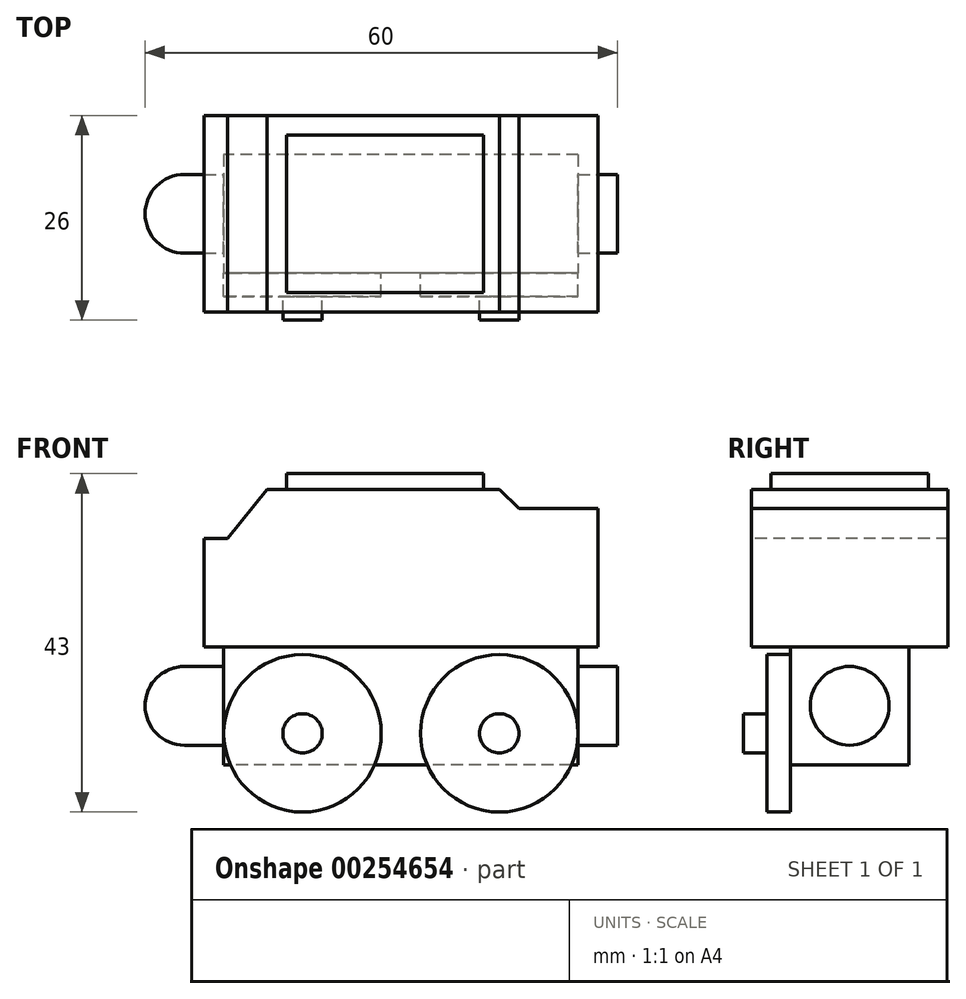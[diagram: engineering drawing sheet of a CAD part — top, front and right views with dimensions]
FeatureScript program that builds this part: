
annotation { "Feature Type Name" : "Feature", "Feature Type Description" : "" }
export const myFeature = defineFeature(function(context is Context, id is Id, definition is map)
    precondition{}
    {
        {
            var Q0;
            Q0=qCreatedBy(makeId("Top.planeOp"),FACE);
            var sketch = newSketch(context, id + "F0", { "sketchPlane" : qUnion([Q0])});
            skLineSegment(sketch, "E0.bottom", {"start": v(22.5, 7.5) * mm, "end": v(-22.5, 7.5) * mm});
            skLineSegment(sketch, "E0.top", {"start": v(22.5, -7.5) * mm, "end": v(-22.5, -7.5) * mm});
            skLineSegment(sketch, "E0.left", {"start": v(22.5, 7.5) * mm, "end": v(22.5, -7.5) * mm});
            skLineSegment(sketch, "E0.right", {"start": v(-22.5, 7.5) * mm, "end": v(-22.5, -7.5) * mm});
            skPoint(sketch, "E0.middle", {"position": v(0, 0) * mm});
            skSolve(sketch);
        }
        {
            var Q0;
            Q0 = qSketchRegion(id + "F0", true);
            extrude(context, id + "F1", {"entities" : qUnion([Q0]), "endBound" : BoundingType.SYMMETRIC, "depth" : 15 * mm});
        }
        {
            var Q0;
            Q0=makeQuery(id+"F1.opExtrude","CAP_FACE",FACE,{"disambiguationData":[OSD([sQuery(id+"F0.wireOp",EDGE,"E0.bottom"),sQuery(id+"F0.wireOp",EDGE,"E0.top"),sQuery(id+"F0.wireOp",EDGE,"E0.left"),sQuery(id+"F0.wireOp",EDGE,"E0.right")])],"isStart":false});
            var sketch = newSketch(context, id + "F2", { "sketchPlane" : qUnion([Q0])});
            skLineSegment(sketch, "E1.bottom", {"start": v(25, 12.5) * mm, "end": v(-25, 12.5) * mm});
            skLineSegment(sketch, "E1.top", {"start": v(25, -12.5) * mm, "end": v(-25, -12.5) * mm});
            skLineSegment(sketch, "E1.left", {"start": v(25, 12.5) * mm, "end": v(25, -12.5) * mm});
            skLineSegment(sketch, "E1.right", {"start": v(-25, 12.5) * mm, "end": v(-25, -12.5) * mm});
            skPoint(sketch, "E1.middle", {"position": v(0, 0) * mm});
            skSolve(sketch);
        }
        {
            var Q0;
            Q0 = qSketchRegion(id + "F2", true);
            extrude(context, id + "F3", {"entities" : qUnion([Q0]), "operationType" : NewBodyOperationType.ADD, "depth" : 20 * mm});
        }
        {
            var Q0;
            Q0=makeQuery(id+"F3.opExtrude","SWEPT_FACE",FACE,{"disambiguationData":[OSD([sQuery(id+"F2.wireOp",EDGE,"E1.top")])]});
            var sketch = newSketch(context, id + "F4", { "sketchPlane" : qUnion([Q0])});
            skLineSegment(sketch, "E2", {"start": v(12.5, 27.5) * mm, "end": v(15, 25.05) * mm});
            skLineSegment(sketch, "E3", {"start": v(15, 25.05) * mm, "end": v(25, 25.05) * mm});
            skLineSegment(sketch, "E4", {"start": v(25, 25.05) * mm, "end": v(25, 27.5) * mm});
            skLineSegment(sketch, "E5", {"start": v(25, 27.5) * mm, "end": v(12.5, 27.5) * mm});
            skSolve(sketch);
        }
        {
            var Q0;
            Q0 = qSketchRegion(id + "F4", true);
            var Q1;
            Q1=makeQuery(id+"F3.opExtrude","SWEPT_FACE",FACE,{"disambiguationData":[OSD([sQuery(id+"F2.wireOp",EDGE,"E1.bottom")])]});
            extrude(context, id + "F5", {"entities" : qUnion([Q0]), "operationType" : NewBodyOperationType.REMOVE, "endBound" : BoundingType.UP_TO_SURFACE, "oppositeDirection" : true, "endBoundEntityFace" : qUnion([Q1]), "depth" : 25 * mm});
        }
        {
            var Q0;
            Q0=makeQuery(id+"F3.opExtrude","SWEPT_FACE",FACE,{"disambiguationData":[OSD([sQuery(id+"F2.wireOp",EDGE,"E1.top")])]});
            var sketch = newSketch(context, id + "F6", { "sketchPlane" : qUnion([Q0])});
            skLineSegment(sketch, "E6", {"start": v(-25, 21.26) * mm, "end": v(-22, 21.26) * mm});
            skLineSegment(sketch, "E7", {"start": v(-22, 21.26) * mm, "end": v(-17, 27.5) * mm});
            skLineSegment(sketch, "E8", {"start": v(-17, 27.5) * mm, "end": v(-25, 27.5) * mm});
            skLineSegment(sketch, "E9", {"start": v(-25, 27.5) * mm, "end": v(-25, 21.26) * mm});
            skSolve(sketch);
        }
        {
            var Q0;
            Q0 = qSketchRegion(id + "F6", true);
            var Q1;
            Q1=makeQuery(id+"F3.opExtrude","SWEPT_FACE",FACE,{"disambiguationData":[OSD([sQuery(id+"F2.wireOp",EDGE,"E1.bottom")])]});
            extrude(context, id + "F7", {"entities" : qUnion([Q0]), "operationType" : NewBodyOperationType.REMOVE, "endBound" : BoundingType.UP_TO_SURFACE, "oppositeDirection" : true, "endBoundEntityFace" : qUnion([Q1]), "depth" : 25 * mm});
        }
        {
            var Q0;
            Q0=makeQuery(id+"F3.opExtrude","CAP_FACE",FACE,{"disambiguationData":[OSD([sQuery(id+"F2.wireOp",EDGE,"E1.bottom"),sQuery(id+"F2.wireOp",EDGE,"E1.top"),sQuery(id+"F2.wireOp",EDGE,"E1.left"),sQuery(id+"F2.wireOp",EDGE,"E1.right")])],"isStart":false});
            var sketch = newSketch(context, id + "F8", { "sketchPlane" : qUnion([Q0])});
            skLineSegment(sketch, "E10.bottom", {"start": v(-14.5, 10) * mm, "end": v(10.5, 10) * mm});
            skLineSegment(sketch, "E10.top", {"start": v(-14.5, -10) * mm, "end": v(10.5, -10) * mm});
            skLineSegment(sketch, "E10.left", {"start": v(-14.5, 10) * mm, "end": v(-14.5, -10) * mm});
            skLineSegment(sketch, "E10.right", {"start": v(10.5, 10) * mm, "end": v(10.5, -10) * mm});
            skSolve(sketch);
        }
        {
            var Q0;
            Q0 = qSketchRegion(id + "F8", true);
            extrude(context, id + "F9", {"entities" : qUnion([Q0]), "operationType" : NewBodyOperationType.ADD, "depth" : 2 * mm});
        }
        {
            var Q0;
            Q0=qCreatedBy(makeId("Front.planeOp"),FACE);
            var sketch = newSketch(context, id + "F10", { "sketchPlane" : qUnion([Q0])});
            skLineSegment(sketch, "E11", {"start": v(49.97, 0) * mm, "end": v(-66.93, 0) * mm, "construction": true});
            skSolve(sketch);
        }
        {
            var Q0;
            Q0=qCreatedBy(makeId("Front.planeOp"),FACE);
            var sketch = newSketch(context, id + "F11", { "sketchPlane" : qUnion([Q0])});
            skLineSegment(sketch, "E12.bottom", {"start": v(22.5, 0) * mm, "end": v(27.5, 0) * mm});
            skLineSegment(sketch, "E12.top", {"start": v(22.5, -5) * mm, "end": v(27.5, -5) * mm});
            skLineSegment(sketch, "E12.left", {"start": v(22.5, 0) * mm, "end": v(22.5, -5) * mm});
            skLineSegment(sketch, "E12.right", {"start": v(27.5, 0) * mm, "end": v(27.5, -5) * mm});
            skSolve(sketch);
        }
        {
            var Q0;
            Q0 = qSketchRegion(id + "F11", true);
            var Q1;
            Q1=sQuery(id+"F10.wireOp",EDGE,"E11");
            revolve(context, id + "F12", {"operationType" : NewBodyOperationType.ADD, "entities" : qUnion([Q0]), "axis" : qUnion([Q1]), "revolveType" : RevolveType.FULL});
        }
        {
            var Q0;
            Q0=qCreatedBy(makeId("Front.planeOp"),FACE);
            var sketch = newSketch(context, id + "F13", { "sketchPlane" : qUnion([Q0])});
            skLineSegment(sketch, "E13.bottom", {"start": v(-22.5, 0) * mm, "end": v(-27.5, 0) * mm});
            skLineSegment(sketch, "E13.top", {"start": v(-22.5, -5) * mm, "end": v(-27.5, -5) * mm});
            skLineSegment(sketch, "E13.left", {"start": v(-22.5, 0) * mm, "end": v(-22.5, -5) * mm});
            skLineSegment(sketch, "E13.right", {"start": v(-27.5, 0) * mm, "end": v(-27.5, -5) * mm});
            skSolve(sketch);
        }
        {
            var Q0;
            Q0 = qSketchRegion(id + "F13", true);
            var Q1;
            Q1=sQuery(id+"F10.wireOp",EDGE,"E11");
            revolve(context, id + "F14", {"operationType" : NewBodyOperationType.ADD, "entities" : qUnion([Q0]), "axis" : qUnion([Q1]), "revolveType" : RevolveType.FULL});
        }
        {
            var Q0;
            Q0=makeQuery(id+"F1.opExtrude","SWEPT_FACE",FACE,{"disambiguationData":[OSD([sQuery(id+"F0.wireOp",EDGE,"E0.top")])]});
            var sketch = newSketch(context, id + "F15", { "sketchPlane" : qUnion([Q0])});
            skCircle(sketch, "E14", {"center": v(-12.5, -3.5) * mm, "radius": 10 * mm});
            skSolve(sketch);
        }
        {
            var Q0;
            Q0 = qSketchRegion(id + "F15", true);
            extrude(context, id + "F16", {"entities" : qUnion([Q0]), "operationType" : NewBodyOperationType.ADD, "depth" : 3 * mm});
        }
        {
            var Q0;
            {var subQ0=sQuery(id+"F0.wireOp",EDGE,"E0.right");var subQ1=sQuery(id+"F0.wireOp",EDGE,"E0.left");var subQ2=sQuery(id+"F0.wireOp",EDGE,"E0.top");var subQ3=makeQuery(id+"F1.opExtrude","SWEPT_FACE",FACE,{"disambiguationData":[OSD([subQ2])]});var subQ4=sQuery(id+"F15.wireOp",EDGE,"E14");Q0=makeQuery(id+"F16.boolean.opBoolean","SPLIT",FACE,{"disambiguationData":[TD([makeQuery(id+"F1.opExtrude","CAP_FACE",FACE,{"disambiguationData":[OSD([sQuery(id+"F0.wireOp",EDGE,"E0.bottom"),subQ2,subQ1,subQ0])],"isStart":true}),subQ3,makeQuery(id+"F1.opExtrude","SWEPT_FACE",FACE,{"disambiguationData":[OSD([subQ1])]}),makeQuery(id+"F1.opExtrude","SWEPT_FACE",FACE,{"disambiguationData":[OSD([subQ0])]}),makeQuery(id+"F3.opExtrude","CAP_FACE",FACE,{"disambiguationData":[OSD([sQuery(id+"F2.wireOp",EDGE,"E1.bottom"),sQuery(id+"F2.wireOp",EDGE,"E1.top"),sQuery(id+"F2.wireOp",EDGE,"E1.left"),sQuery(id+"F2.wireOp",EDGE,"E1.right")])],"isStart":true}),makeQuery(id+"F16.opExtrude","SWEPT_FACE",FACE,{"disambiguationData":[OSD([subQ4])]}),makeQuery(id+"F16.opExtrude","CAP_FACE",FACE,{"disambiguationData":[OSD([subQ4])],"isStart":true})])],"derivedFrom":subQ3});}
            var sketch = newSketch(context, id + "F17", { "sketchPlane" : qUnion([Q0])});
            skCircle(sketch, "E15", {"center": v(12.5, -3.5) * mm, "radius": 10 * mm});
            skSolve(sketch);
        }
        {
            var Q0;
            Q0 = qSketchRegion(id + "F17", true);
            extrude(context, id + "F18", {"entities" : qUnion([Q0]), "operationType" : NewBodyOperationType.ADD, "depth" : 3 * mm});
        }
        {
            var Q0;
            Q0=makeQuery(id+"F16.opExtrude","CAP_FACE",FACE,{"disambiguationData":[OSD([sQuery(id+"F15.wireOp",EDGE,"E14")])],"isStart":false});
            var sketch = newSketch(context, id + "F19", { "sketchPlane" : qUnion([Q0])});
            skCircle(sketch, "E16", {"center": v(-12.5, -3.5) * mm, "radius": 2.5 * mm});
            skSolve(sketch);
        }
        {
            var Q0;
            Q0 = qSketchRegion(id + "F19", true);
            extrude(context, id + "F20", {"entities" : qUnion([Q0]), "operationType" : NewBodyOperationType.ADD, "depth" : 3 * mm});
        }
        {
            var Q0;
            Q0=makeQuery(id+"F18.opExtrude","CAP_FACE",FACE,{"disambiguationData":[OSD([sQuery(id+"F17.wireOp",EDGE,"E15")])],"isStart":false});
            var sketch = newSketch(context, id + "F21", { "sketchPlane" : qUnion([Q0])});
            skCircle(sketch, "E17", {"center": v(12.5, -3.5) * mm, "radius": 2.5 * mm});
            skSolve(sketch);
        }
        {
            var Q0;
            Q0 = qSketchRegion(id + "F21", true);
            extrude(context, id + "F22", {"entities" : qUnion([Q0]), "operationType" : NewBodyOperationType.ADD, "depth" : 3 * mm});
        }
        {
            var Q0;
            Q0=qCreatedBy(makeId("Front.planeOp"),FACE);
            var sketch = newSketch(context, id + "F23", { "sketchPlane" : qUnion([Q0])});
            skArc(sketch, "E18", {"start": v(-27.5, 5) * mm, "mid": v(-31.04, 3.54) * mm, "end": v(-32.5, 0) * mm});
            skLineSegment(sketch, "E19", {"start": v(-32.5, 0) * mm, "end": v(-27.5, 0) * mm});
            skLineSegment(sketch, "E20", {"start": v(-27.5, 0) * mm, "end": v(-27.5, 5) * mm});
            skSolve(sketch);
        }
        {
            var Q0;
            Q0 = qSketchRegion(id + "F23", true);
            var Q1;
            Q1=sQuery(id+"F23.wireOp",EDGE,"E19");
            revolve(context, id + "F24", {"operationType" : NewBodyOperationType.ADD, "entities" : qUnion([Q0]), "axis" : qUnion([Q1]), "revolveType" : RevolveType.FULL});
        }
    });
